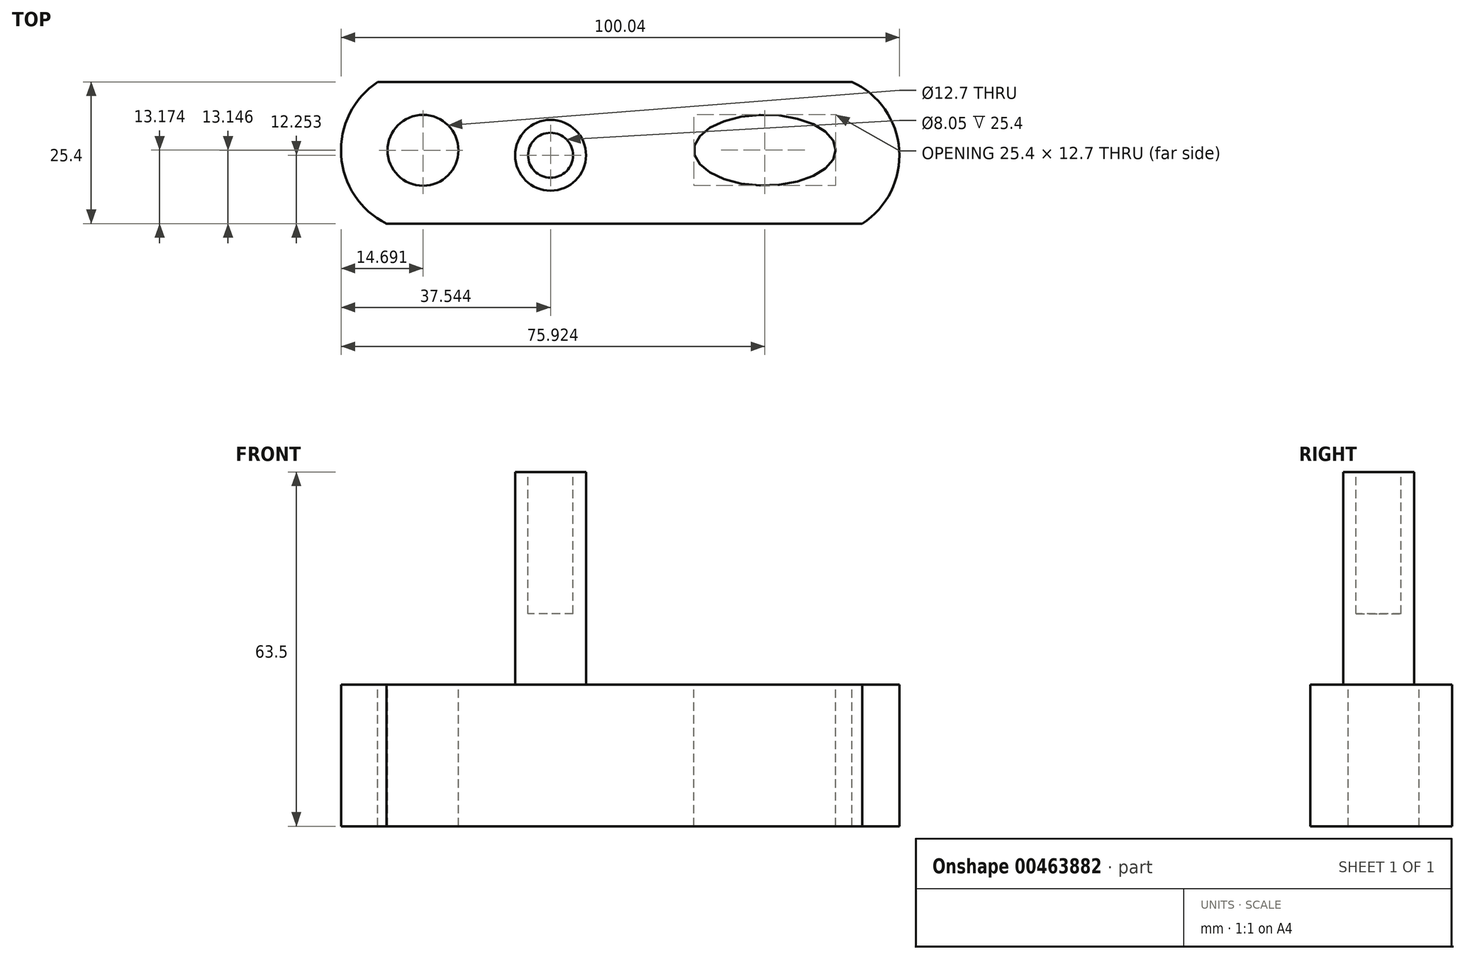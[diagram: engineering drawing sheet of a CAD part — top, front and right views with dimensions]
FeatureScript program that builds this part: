
annotation { "Feature Type Name" : "Feature", "Feature Type Description" : "" }
export const myFeature = defineFeature(function(context is Context, id is Id, definition is map)
    precondition{}
    {
        {
            var Q0;
            Q0=qCreatedBy(makeId("Front.planeOp"),FACE);
            var sketch = newSketch(context, id + "F0", { "sketchPlane" : qUnion([Q0])});
            skLineSegment(sketch, "E0", {"start": v(0, 0) * mm, "end": v(0, 25.4) * mm});
            skLineSegment(sketch, "E1", {"start": v(0, 25.4) * mm, "end": v(101.6, 25.4) * mm});
            skLineSegment(sketch, "E2", {"start": v(101.6, 25.4) * mm, "end": v(101.6, 0) * mm});
            skLineSegment(sketch, "E3", {"start": v(101.6, 0) * mm, "end": v(0, 0) * mm});
            skSolve(sketch);
        }
        {
            var Q0;
            Q0 = qSketchRegion(id + "F0", true);
            extrude(context, id + "F1", {"entities" : qUnion([Q0]), "depth" : 25.4 * mm});
        }
        {
            var Q0;
            Q0=makeQuery(id+"F1.opExtrude","SWEPT_FACE",FACE,{"disambiguationData":[OSD([sQuery(id+"F0.wireOp",EDGE,"E1")])]});
            var sketch = newSketch(context, id + "F2", { "sketchPlane" : qUnion([Q0])});
            skArc(sketch, "E4", {"start": v(94.1, -25.4) * mm, "mid": v(100.74, -12.15) * mm, "end": v(92.25, 0) * mm});
            skSolve(sketch);
        }
        {
            var Q0;
            {var subQ0=sQuery(id+"F2.wireOp",EDGE,"E4");Q0=makeQuery(id+"F2.imprint","IMPRINT",FACE,{"disambiguationData":[TD([[makeQuery(id+"F2.imprint","IMPRINT",EDGE,{"derivedFrom":subQ0}),-1.0]])]});}
            extrude(context, id + "F3", {"entities" : qUnion([Q0]), "operationType" : NewBodyOperationType.REMOVE, "oppositeDirection" : true, "depth" : 25.4 * mm});
        }
        {
            var Q0;
            Q0=makeQuery(id+"F1.opExtrude","SWEPT_FACE",FACE,{"disambiguationData":[OSD([sQuery(id+"F0.wireOp",EDGE,"E1")])]});
            var sketch = newSketch(context, id + "F4", { "sketchPlane" : qUnion([Q0])});
            skArc(sketch, "E5", {"start": v(7.33, 0) * mm, "mid": v(0.77, -13.15) * mm, "end": v(8.88, -25.4) * mm});
            skSolve(sketch);
        }
        {
            var Q0;
            {var subQ0=sQuery(id+"F4.wireOp",EDGE,"E5");Q0=makeQuery(id+"F4.imprint","IMPRINT",FACE,{"disambiguationData":[TD([[makeQuery(id+"F4.imprint","IMPRINT",EDGE,{"derivedFrom":subQ0}),-1.0]])]});}
            extrude(context, id + "F5", {"entities" : qUnion([Q0]), "operationType" : NewBodyOperationType.REMOVE, "oppositeDirection" : true, "depth" : 25.4 * mm});
        }
        {
            var Q0;
            Q0=makeQuery(id+"F1.opExtrude","SWEPT_FACE",FACE,{"disambiguationData":[OSD([sQuery(id+"F0.wireOp",EDGE,"E1")])]});
            var sketch = newSketch(context, id + "F6", { "sketchPlane" : qUnion([Q0])});
            skCircle(sketch, "E6", {"center": v(15.43, -12.25) * mm, "radius": 6.35 * mm});
            skSolve(sketch);
        }
        {
            var Q0;
            Q0 = qSketchRegion(id + "F6", true);
            extrude(context, id + "F7", {"entities" : qUnion([Q0]), "operationType" : NewBodyOperationType.REMOVE, "oppositeDirection" : true, "depth" : 25.4 * mm});
        }
        {
            var Q0;
            Q0=makeQuery(id+"F1.opExtrude","SWEPT_FACE",FACE,{"disambiguationData":[OSD([sQuery(id+"F0.wireOp",EDGE,"E1")])]});
            var sketch = newSketch(context, id + "F8", { "sketchPlane" : qUnion([Q0])});
            skEllipse(sketch, "E7", {"center": v(76.66, -12.23) * mm, "majorRadius": 12.7 * mm, "minorRadius": 6.35 * mm, "majorAxis": v(1, 0)});
            skSolve(sketch);
        }
        {
            var Q0;
            Q0=makeQuery(id+"F8.imprint","IMPRINT",FACE,{"disambiguationData":[TD([[makeQuery(id+"F8.imprint","IMPRINT",EDGE,{"derivedFrom":sQuery(id+"F8.wireOp",EDGE,"E7")}),1.0]])]});
            extrude(context, id + "F9", {"entities" : qUnion([Q0]), "operationType" : NewBodyOperationType.REMOVE, "oppositeDirection" : true, "depth" : 25.4 * mm});
        }
        {
            var Q0;
            Q0=makeQuery(id+"F1.opExtrude","SWEPT_FACE",FACE,{"disambiguationData":[OSD([sQuery(id+"F0.wireOp",EDGE,"E1")])]});
            var sketch = newSketch(context, id + "F10", { "sketchPlane" : qUnion([Q0])});
            skCircle(sketch, "E8", {"center": v(38.28, -13.15) * mm, "radius": 6.35 * mm});
            skPoint(sketch, "E8.centerSnap0", {"position": v(0.77, -13.15) * mm});
            skSolve(sketch);
        }
        {
            var Q0;
            Q0 = qSketchRegion(id + "F10", true);
            extrude(context, id + "F11", {"entities" : qUnion([Q0]), "operationType" : NewBodyOperationType.ADD, "depth" : 38.1 * mm});
        }
        {
            var Q0;
            Q0=makeQuery(id+"F11.opExtrude","CAP_FACE",FACE,{"disambiguationData":[OSD([sQuery(id+"F10.wireOp",EDGE,"E8")])],"isStart":false});
            var sketch = newSketch(context, id + "F12", { "sketchPlane" : qUnion([Q0])});
            skCircle(sketch, "E9", {"center": v(38.28, -13.15) * mm, "radius": 4.03 * mm});
            skSolve(sketch);
        }
        {
            var Q0;
            Q0=makeQuery(id+"F12.imprint","IMPRINT",FACE,{"disambiguationData":[TD([[makeQuery(id+"F12.imprint","IMPRINT",EDGE,{"derivedFrom":sQuery(id+"F12.wireOp",EDGE,"E9")}),1.0]])]});
            extrude(context, id + "F13", {"entities" : qUnion([Q0]), "operationType" : NewBodyOperationType.REMOVE, "oppositeDirection" : true, "depth" : 25.4 * mm});
        }
    });
